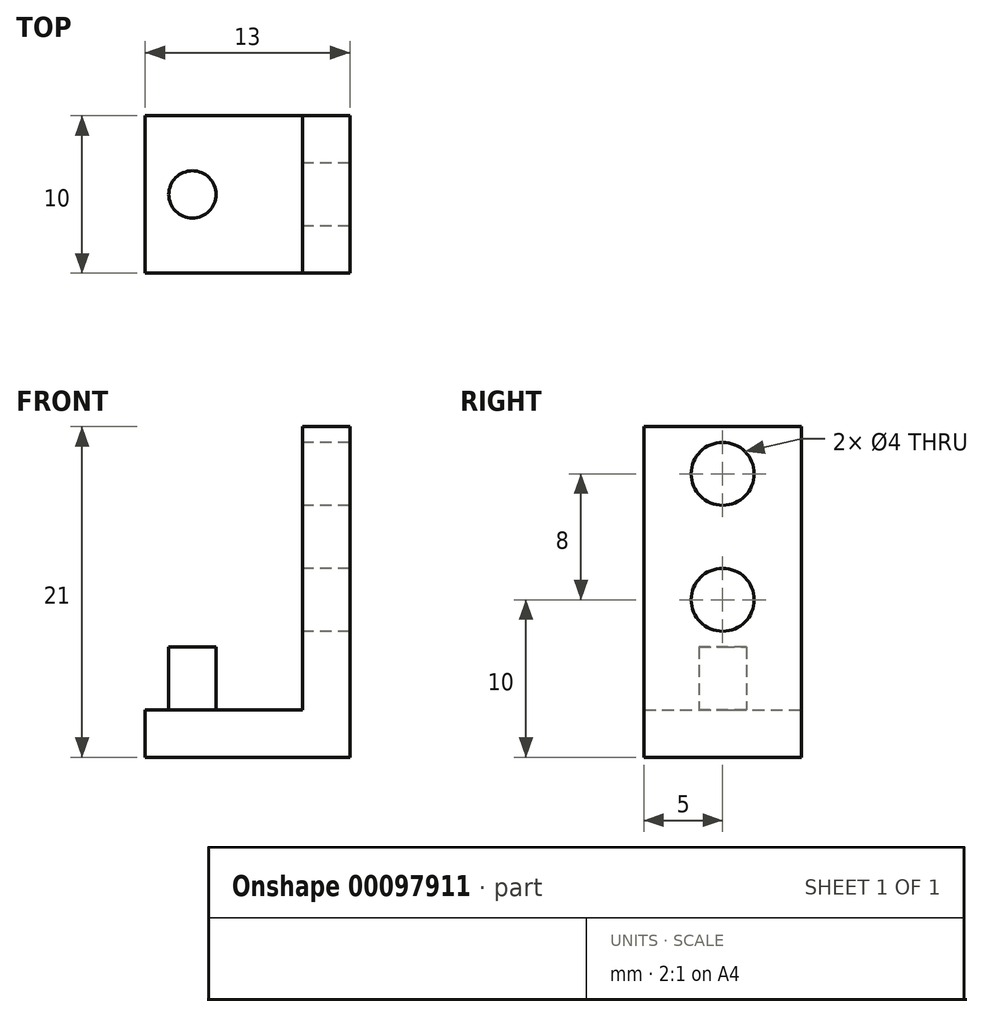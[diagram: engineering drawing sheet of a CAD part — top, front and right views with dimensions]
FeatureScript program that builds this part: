
annotation { "Feature Type Name" : "Feature", "Feature Type Description" : "" }
export const myFeature = defineFeature(function(context is Context, id is Id, definition is map)
    precondition{}
    {
        {
            var Q0;
            Q0=qCreatedBy(makeId("Front.planeOp"),FACE);
            var sketch = newSketch(context, id + "F0", { "sketchPlane" : qUnion([Q0])});
            skLineSegment(sketch, "E0", {"start": v(0, 0) * mm, "end": v(-13, 0) * mm});
            skLineSegment(sketch, "E1", {"start": v(-13, 0) * mm, "end": v(-13, 3) * mm});
            skLineSegment(sketch, "E2", {"start": v(-13, 3) * mm, "end": v(-3, 3) * mm});
            skLineSegment(sketch, "E3", {"start": v(-3, 3) * mm, "end": v(-3, 21) * mm});
            skLineSegment(sketch, "E4", {"start": v(-3, 21) * mm, "end": v(0, 21) * mm});
            skLineSegment(sketch, "E5", {"start": v(0, 21) * mm, "end": v(0, 0) * mm});
            skSolve(sketch);
        }
        {
            var Q0;
            Q0=makeQuery(id+"F0.imprint","IMPRINT",FACE,{"disambiguationData":[TD([[makeQuery(id+"F0.imprint","IMPRINT",EDGE,{"derivedFrom":sQuery(id+"F0.wireOp",EDGE,"E0")}),-1.0]])]});
            extrude(context, id + "F1", {"entities" : qUnion([Q0]), "depth" : 10 * mm});
        }
        {
            var Q0;
            Q0=makeQuery(id+"F1.opExtrude","SWEPT_FACE",FACE,{"disambiguationData":[OSD([sQuery(id+"F0.wireOp",EDGE,"E3")])]});
            var sketch = newSketch(context, id + "F2", { "sketchPlane" : qUnion([Q0])});
            skCircle(sketch, "E6", {"center": v(5, 18) * mm, "radius": 2 * mm});
            skPoint(sketch, "E6.centerSnap0", {"position": v(5, 21) * mm});
            skCircle(sketch, "E7", {"center": v(5, 10) * mm, "radius": 2 * mm});
            skSolve(sketch);
        }
        {
            var Q0;
            Q0=makeQuery(id+"F2.imprint","IMPRINT",FACE,{"disambiguationData":[TD([[makeQuery(id+"F2.imprint","IMPRINT",EDGE,{"derivedFrom":sQuery(id+"F2.wireOp",EDGE,"E6")}),1.0]])]});
            var Q1;
            Q1=makeQuery(id+"F2.imprint","IMPRINT",FACE,{"disambiguationData":[TD([[makeQuery(id+"F2.imprint","IMPRINT",EDGE,{"derivedFrom":sQuery(id+"F2.wireOp",EDGE,"E7")}),1.0]])]});
            extrude(context, id + "F3", {"entities" : qUnion([Q0, Q1]), "operationType" : NewBodyOperationType.REMOVE, "oppositeDirection" : true, "depth" : 25 * mm});
        }
        {
            var Q0;
            Q0=makeQuery(id+"F1.opExtrude","SWEPT_FACE",FACE,{"disambiguationData":[OSD([sQuery(id+"F0.wireOp",EDGE,"E2")])]});
            var sketch = newSketch(context, id + "F4", { "sketchPlane" : qUnion([Q0])});
            skCircle(sketch, "E8", {"center": v(-10, -5) * mm, "radius": 1.5 * mm});
            skPoint(sketch, "E8.centerSnap0", {"position": v(-13, -5) * mm});
            skSolve(sketch);
        }
        {
            var Q0;
            Q0=makeQuery(id+"F4.imprint","IMPRINT",FACE,{"disambiguationData":[TD([[makeQuery(id+"F4.imprint","IMPRINT",EDGE,{"derivedFrom":sQuery(id+"F4.wireOp",EDGE,"E8")}),1.0]])]});
            extrude(context, id + "F5", {"entities" : qUnion([Q0]), "operationType" : NewBodyOperationType.ADD, "depth" : 4 * mm});
        }
    });
